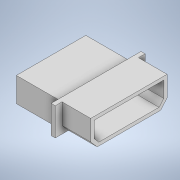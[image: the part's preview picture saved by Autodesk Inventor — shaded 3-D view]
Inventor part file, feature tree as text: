
AUTODESK INVENTOR PART (.ipt)
format: ipt  version: 2021 (Build 250183000, 183)  size: 166,912 bytes
history: native  units: in
note: dims shown in document units (in); Inventor stores cm internally (conversion verified against a paired STEP export)
features: extrude x6, sketch x6, projected_geometry x1
ambient origin geometry x8: Origin, YZ Plane, XZ Plane, XY Plane, X Axis, Y Axis, Z Axis, Center Point
bodies: Solid1 (feature_tree)
feature tree (13):
  extrude  "Extrusion1"  Depth=0.934in
  extrude  "Extrusion2"  Depth=0.54in
  extrude  "Extrusion3"  Depth=0.042in
  extrude  "Extrusion4"  Depth=0.042in
  extrude  "Extrusion5"  Depth=1.08in
  extrude  "Extrusion6"  Depth=0.0815in
  sketch  "Sketch1"  dims[d0=0.917in d1=0.934in]
  sketch  "Sketch2"  dims[d2=0.335in d3=0.0in d4=0.54in]
  sketch  "Sketch3"  dims[d5=0.041in d6=0.0in d7=0.042in]
  sketch  "Sketch4"  dims[d8=0.833in d9=0.042in]
  sketch  "Sketch5"  dims[d10=0.041in d11=0.0in d12=1.08in]
  sketch  "Sketch6"  dims[d13=0.0815in d14=0.0815in d15=0.05in d16=0.0in d17=0.761in d20=0.245in d21=0.9557in d22=0.9557in d23=0.05in d24=0.0in d25=0.04in d26=0.05in d27=0.0in]
  projected_geometry  "Projected Loop1"
